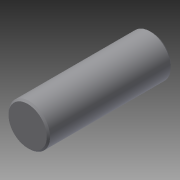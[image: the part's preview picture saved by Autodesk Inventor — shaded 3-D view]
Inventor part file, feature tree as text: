
AUTODESK INVENTOR PART (.ipt)
format: ipt  version: 2014 SP2 (Build 180246200, 246)  size: 101,888 bytes
history: native  units: in
note: dims shown in document units (in); Inventor stores cm internally (conversion verified against a paired STEP export)
features: other x35, revolve x1, sketch x1
ambient origin geometry x8: Origin, YZ Plane, XZ Plane, XY Plane, X Axis, Y Axis, Z Axis, Center Point
bodies: Solid1 (feature_tree)
feature tree (37):
  revolve  "Revolution1"  [1 undecoded]
  other  "dia1_XY"
  other  "dia1_YZ"
  other  "dia1_ZX"
  other  "dia1_X"
  other  "dia1_Y"
  other  "dia1_Z"
  other  "dia1_Center"
  other  "dia2_XY"
  other  "dia2_YZ"
  other  "dia2_ZX"
  other  "dia2_X"
  other  "dia2_Y"
  other  "dia2_Z"
  other  "dia2_Center"
  other  "pin_XY"
  other  "pin_YZ"
  other  "pin_ZX"
  other  "pin_X"
  other  "pin_Y"
  other  "pin_Z"
  other  "pin_Center"
  other  "pin1_XY"
  other  "pin1_YZ"
  other  "pin1_ZX"
  other  "pin1_X"
  other  "pin1_Y"
  other  "pin1_Z"
  other  "pin1_Center"
  other  "pin2_XY"
  other  "pin2_YZ"
  other  "pin2_ZX"
  other  "pin2_X"
  other  "pin2_Y"
  other  "pin2_Z"
  other  "pin2_Center"
  sketch  "Sketch_1"  dims[d0=360.0deg]
note: 1 required parameter value undecoded (feature->parameter linkage not recoverable at this tier; creation-order binding heuristic only, values carry confidence <= 0.55)
